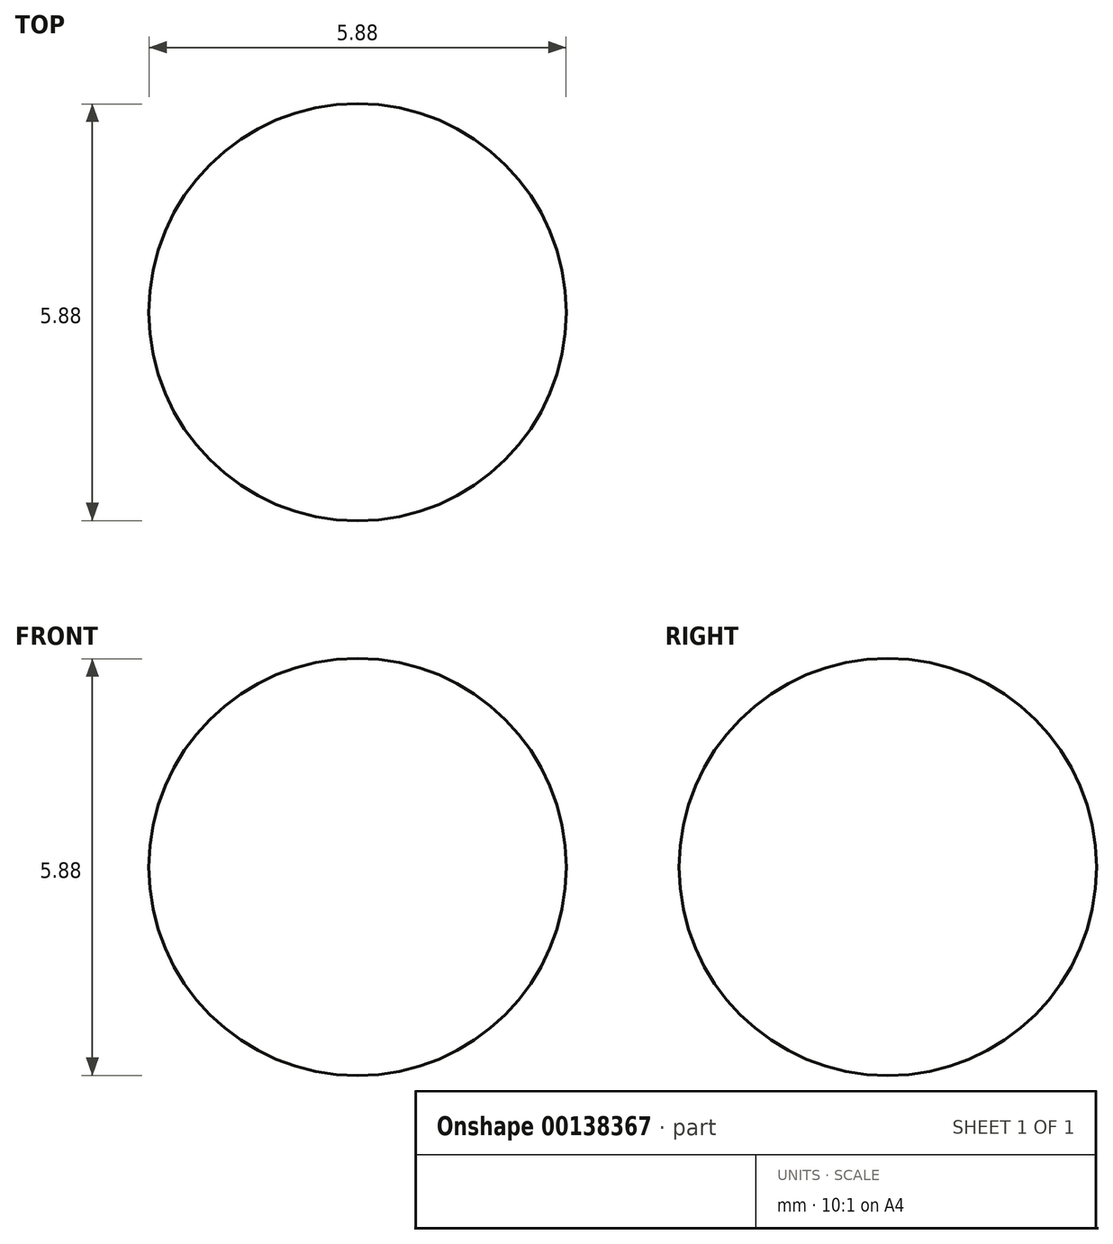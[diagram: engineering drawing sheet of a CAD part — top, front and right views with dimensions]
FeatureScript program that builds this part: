
annotation { "Feature Type Name" : "Feature", "Feature Type Description" : "" }
export const myFeature = defineFeature(function(context is Context, id is Id, definition is map)
    precondition{}
    {
        {
            var Q0;
            Q0=qCreatedBy(makeId("Front.planeOp"),FACE);
            var sketch = newSketch(context, id + "F0", { "sketchPlane" : qUnion([Q0])});
            skArc(sketch, "E0", {"start": v(0, 2.94) * mm, "mid": v(-2.94, 0) * mm, "end": v(0, -2.94) * mm});
            skLineSegment(sketch, "E1", {"start": v(0, 2.94) * mm, "end": v(0, -2.94) * mm});
            skSolve(sketch);
        }
        {
            var Q0;
            Q0 = qSketchRegion(id + "F0", true);
            var Q1;
            Q1=sQuery(id+"F0.wireOp",EDGE,"E1");
            revolve(context, id + "F1", {"entities" : qUnion([Q0]), "axis" : qUnion([Q1]), "revolveType" : RevolveType.FULL});
        }
    });
